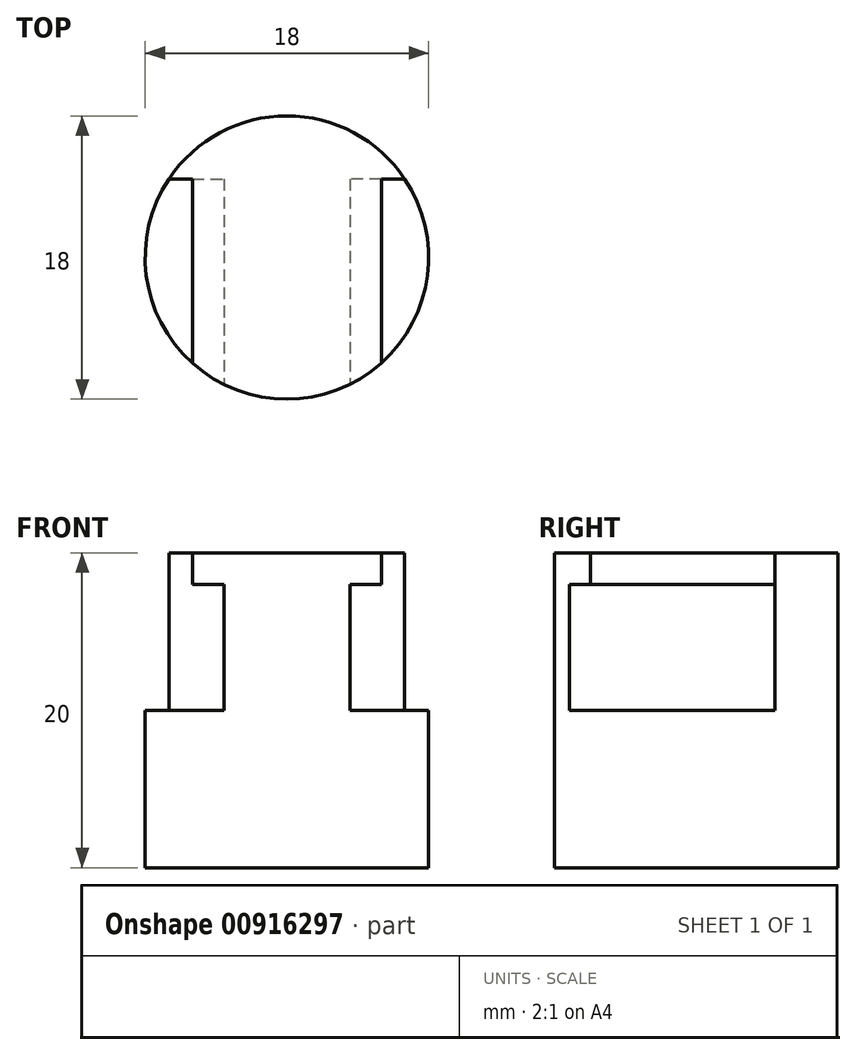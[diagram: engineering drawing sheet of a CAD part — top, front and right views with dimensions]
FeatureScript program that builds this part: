
annotation { "Feature Type Name" : "Feature", "Feature Type Description" : "" }
export const myFeature = defineFeature(function(context is Context, id is Id, definition is map)
    precondition{}
    {
        {
            var Q0;
            Q0=qCreatedBy(makeId("Top.planeOp"),FACE);
            var sketch = newSketch(context, id + "F0", { "sketchPlane" : qUnion([Q0])});
            skCircle(sketch, "E0", {"center": v(0, 0) * mm, "radius": 9 * mm});
            skSolve(sketch);
        }
        {
            var Q0;
            Q0 = qSketchRegion(id + "F0", true);
            extrude(context, id + "F1", {"entities" : qUnion([Q0]), "depth" : 20 * mm, "offsetDistance" : 25 * mm});
        }
        {
            var Q0;
            Q0=qCreatedBy(makeId("Front.planeOp"),FACE);
            var sketch = newSketch(context, id + "F2", { "sketchPlane" : qUnion([Q0])});
            skLineSegment(sketch, "E1", {"start": v(0, 20) * mm, "end": v(-6, 20) * mm});
            skLineSegment(sketch, "E2", {"start": v(-6, 20) * mm, "end": v(-6, 18) * mm});
            skLineSegment(sketch, "E3", {"start": v(-6, 18) * mm, "end": v(-4, 18) * mm});
            skLineSegment(sketch, "E4", {"start": v(-4, 18) * mm, "end": v(-4, 10) * mm});
            skLineSegment(sketch, "E5", {"start": v(-4, 10) * mm, "end": v(0, 10) * mm});
            skLineSegment(sketch, "E6", {"start": v(0, 10) * mm, "end": v(0, 20) * mm});
            skLineSegment(sketch, "E7", {"start": v(-6, 20) * mm, "end": v(-9, 20) * mm});
            skLineSegment(sketch, "E8", {"start": v(-9, 20) * mm, "end": v(-9, 10) * mm});
            skLineSegment(sketch, "E9", {"start": v(-9, 10) * mm, "end": v(-4, 10) * mm});
            skLineSegment(sketch, "E10.MirrorCS", {"start": v(4, 18) * mm, "end": v(4, 10) * mm});
            skLineSegment(sketch, "E11.MirrorCS", {"start": v(6, 18) * mm, "end": v(4, 18) * mm});
            skLineSegment(sketch, "E12.MirrorCS", {"start": v(6, 20) * mm, "end": v(6, 18) * mm});
            skLineSegment(sketch, "E13.MirrorCS", {"start": v(6, 20) * mm, "end": v(9, 20) * mm});
            skLineSegment(sketch, "E14.MirrorCS", {"start": v(9, 20) * mm, "end": v(9, 10) * mm});
            skLineSegment(sketch, "E15.MirrorCS", {"start": v(9, 10) * mm, "end": v(4, 10) * mm});
            skSolve(sketch);
        }
        {
            var Q0;
            Q0=makeQuery(id+"F2.imprint","IMPRINT",FACE,{"disambiguationData":[TD([[makeQuery(id+"F2.imprint","IMPRINT",EDGE,{"derivedFrom":sQuery(id+"F2.wireOp",EDGE,"E10.MirrorCS")}),1.0]])]});
            var Q1;
            Q1=makeQuery(id+"F2.imprint","IMPRINT",FACE,{"disambiguationData":[TD([[makeQuery(id+"F2.imprint","IMPRINT",EDGE,{"derivedFrom":sQuery(id+"F2.wireOp",EDGE,"E3")}),-1.0]])]});
            extrude(context, id + "F3", {"entities" : qUnion([Q0, Q1]), "operationType" : NewBodyOperationType.REMOVE, "oppositeDirection" : true, "depth" : 5 * mm, "offsetDistance" : 25 * mm, "hasSecondDirection" : true, "secondDirectionOppositeDirection" : false, "secondDirectionDepth" : 25 * mm});
        }
    });
